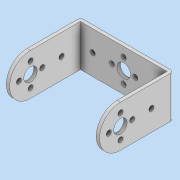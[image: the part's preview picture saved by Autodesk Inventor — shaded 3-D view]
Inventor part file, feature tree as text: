
AUTODESK INVENTOR PART (.ipt)
format: ipt  version: 2021.4 (Build 254397000, 397)  size: 195,072 bytes
history: native  units: in
note: dims shown in document units (in); Inventor stores cm internally (conversion verified against a paired STEP export)
features: sketch x5, extrude x5, hole x2, fillet x1
ambient origin geometry x8: Origin, YZ Plane, XZ Plane, XY Plane, X Axis, Y Axis, Z Axis, Center Point
bodies: Solid1 (feature_tree)
feature tree (13):
  sketch  "Sketch1"  dims[d0=2.0472in d1=0.9843in]
  extrude  "Extrusion1"  Depth=0.9843in
  extrude  "Extrusion2"  Depth=0.1181in
  extrude  "Extrusion3"  Depth=0.1181in
  extrude  "Extrusion4"  Depth=0.1181in
  extrude  "Extrusion5"  Depth=0.0787in
  fillet  "Fillet1"  Radius=1.0236in
  sketch  "Sketch5"  dims[d9=0.2913in d10=0.2913in d11=1.0236in d13=0.0787in d14=0.0787in d15=0.0787in d16=0.0in d17=0.1181in d18=0.0in d19=1.1417in d20=0.0in d22=0.4921in d23=0.0787in d24=0.0in d25=0.0787in d26=0.0in d27=0.0787in d28=0.315in d29=0.5512in d30=1.5748in d32=360.0deg d34=0.1181in d35=0.7323in d36=0.1181in d37=0.2362in d38=0.1575in d39=0.0787in d40=90.0deg d41=0.315in d42=0.8108in d43=0.315in d44=0.2362in d45=0.1575in d46=0.0787in d47=90.0deg d48=0.315in d49=0.8108in]
  hole  "Hole1"  [1 undecoded]
  hole  "Hole2"  [1 undecoded]
  sketch  "Sketch2"  dims[d2=0.1181in d3=0.1181in]
  sketch  "Sketch3"  dims[d4=0.1181in d5=0.1181in]
  sketch  "Sketch4"  dims[d6=0.1181in d7=0.1181in]
note: 2 required parameter values undecoded (feature->parameter linkage not recoverable at this tier; creation-order binding heuristic only, values carry confidence <= 0.55)
